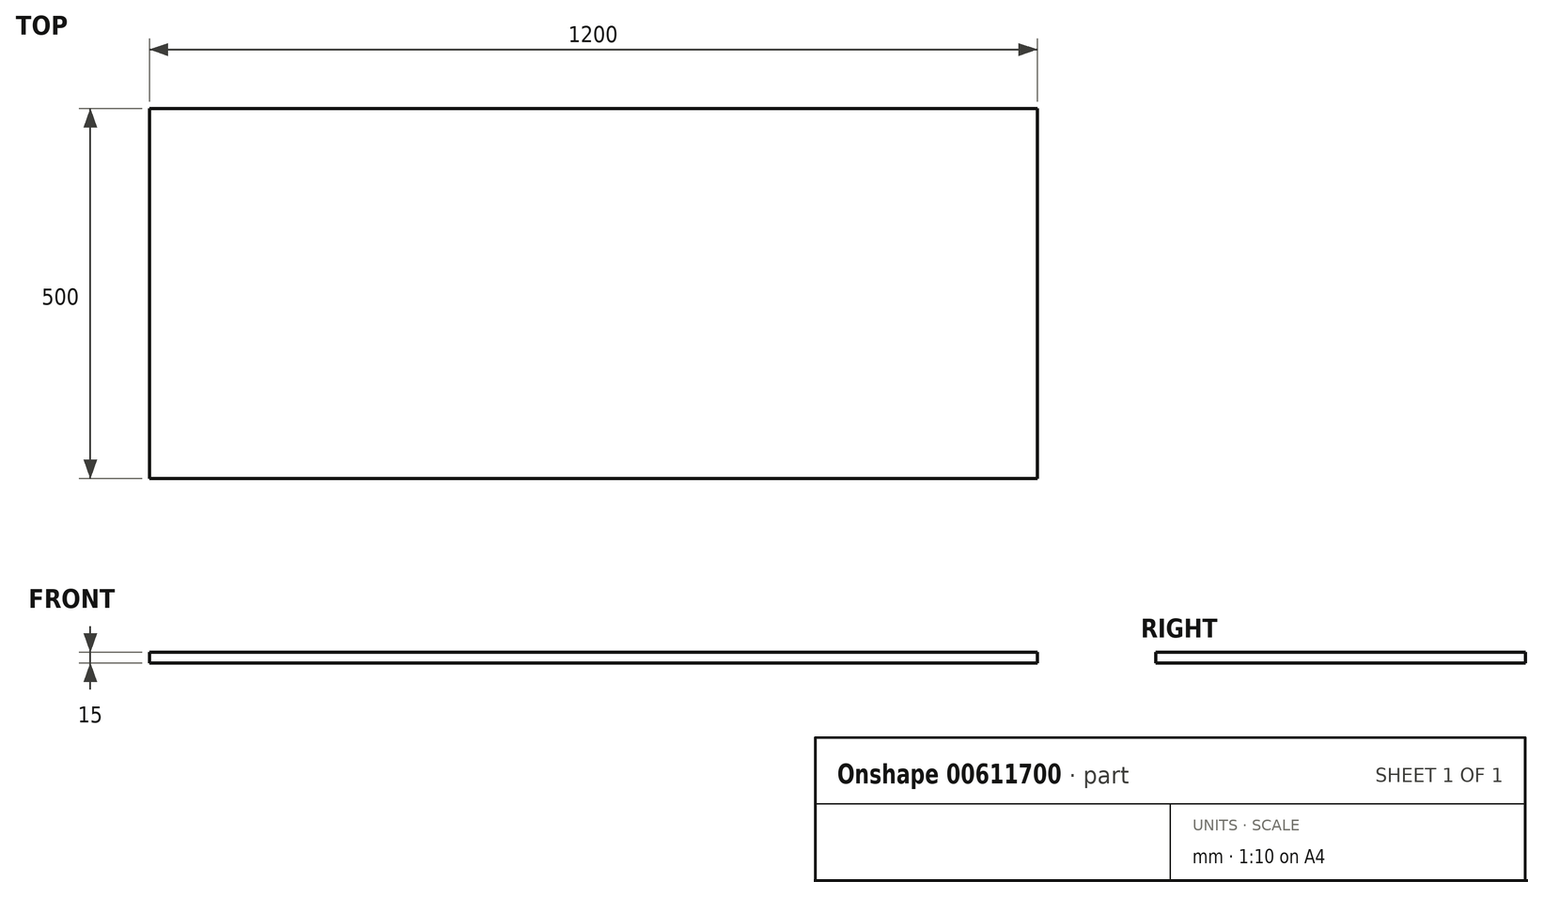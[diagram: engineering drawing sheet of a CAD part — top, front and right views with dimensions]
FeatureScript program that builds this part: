
annotation { "Feature Type Name" : "Feature", "Feature Type Description" : "" }
export const myFeature = defineFeature(function(context is Context, id is Id, definition is map)
    precondition{}
    {
        {
            var Q0;
            Q0=qCreatedBy(makeId("Top.planeOp"),FACE);
            var sketch = newSketch(context, id + "F0", { "sketchPlane" : qUnion([Q0])});
            skLineSegment(sketch, "E0.bottom", {"start": v(-600, 250) * mm, "end": v(600, 250) * mm});
            skLineSegment(sketch, "E0.top", {"start": v(-600, -250) * mm, "end": v(600, -250) * mm});
            skLineSegment(sketch, "E0.left", {"start": v(-600, 250) * mm, "end": v(-600, -250) * mm});
            skLineSegment(sketch, "E0.right", {"start": v(600, 250) * mm, "end": v(600, -250) * mm});
            skPoint(sketch, "E0.middle", {"position": v(0, 0) * mm});
            skSolve(sketch);
        }
        {
            var Q0;
            Q0=makeQuery(id+"F0.imprint","IMPRINT",FACE,{"disambiguationData":[TD([[makeQuery(id+"F0.imprint","IMPRINT",EDGE,{"derivedFrom":sQuery(id+"F0.wireOp",EDGE,"E0.bottom")}),-1.0]])]});
            extrude(context, id + "F1", {"entities" : qUnion([Q0]), "depth" : 15 * mm, "offsetDistance" : 25 * mm});
        }
    });
